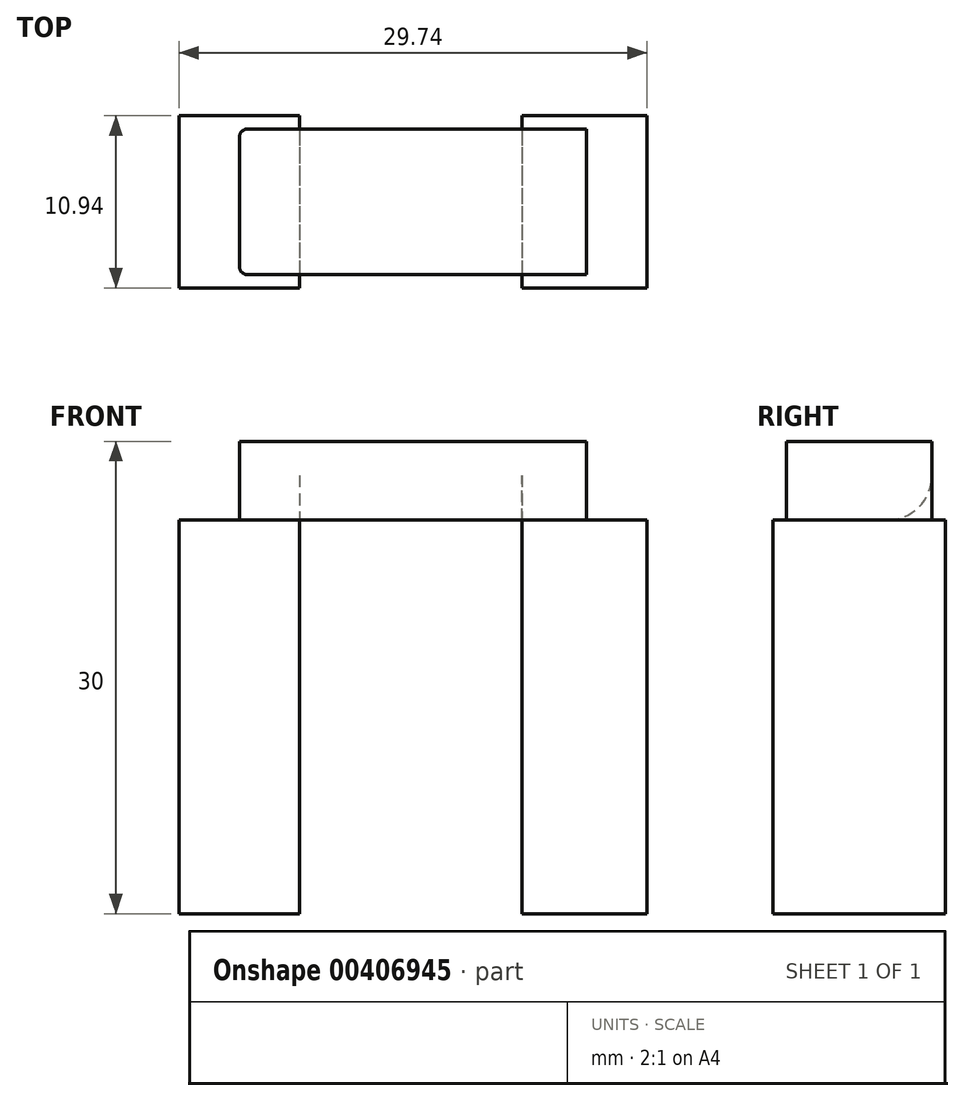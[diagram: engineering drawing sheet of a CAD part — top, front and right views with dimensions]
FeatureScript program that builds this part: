
annotation { "Feature Type Name" : "Feature", "Feature Type Description" : "" }
export const myFeature = defineFeature(function(context is Context, id is Id, definition is map)
    precondition{}
    {
        {
            var Q0;
            Q0=qCreatedBy(makeId("Top.planeOp"),FACE);
            var sketch = newSketch(context, id + "F0", { "sketchPlane" : qUnion([Q0])});
            skLineSegment(sketch, "E0.bottom", {"start": v(11.02, 4.62) * mm, "end": v(-11.02, 4.62) * mm});
            skLineSegment(sketch, "E0.top", {"start": v(11.02, -4.62) * mm, "end": v(-11.02, -4.62) * mm});
            skLineSegment(sketch, "E0.left", {"start": v(11.02, 4.62) * mm, "end": v(11.02, -4.62) * mm});
            skLineSegment(sketch, "E0.right", {"start": v(-11.02, 4.62) * mm, "end": v(-11.02, -4.62) * mm});
            skPoint(sketch, "E0.middle", {"position": v(0, 0) * mm});
            skLineSegment(sketch, "E1.bottom", {"start": v(14.87, 5.47) * mm, "end": v(-14.87, 5.47) * mm});
            skLineSegment(sketch, "E1.top", {"start": v(14.87, -5.47) * mm, "end": v(-14.87, -5.47) * mm});
            skLineSegment(sketch, "E1.left", {"start": v(14.87, 5.47) * mm, "end": v(14.87, -5.47) * mm});
            skLineSegment(sketch, "E1.right", {"start": v(-14.87, 5.47) * mm, "end": v(-14.87, -5.47) * mm});
            skLineSegment(sketch, "E2", {"start": v(-7.22, 5.47) * mm, "end": v(-7.22, -5.47) * mm});
            skLineSegment(sketch, "E3", {"start": v(6.91, 5.47) * mm, "end": v(6.91, -5.47) * mm});
            skSolve(sketch);
        }
        {
            var Q0;
            Q0=makeQuery(id+"F0.imprint","IMPRINT",FACE,{"disambiguationData":[TD([[makeQuery(id+"F0.imprint","IMPRINT",EDGE,{"derivedFrom":sQuery(id+"F0.wireOp",EDGE,"E0.bottom")}),1.0]])]});
            extrude(context, id + "F1", {"entities" : qUnion([Q0]), "depth" : 5 * mm});
        }
        {
            var Q0;
            {var subQ4=sQuery(id+"F0.wireOp",EDGE,"E0.right");Q0=makeQuery(id+"F0.imprint","IMPRINT",FACE,{"disambiguationData":[TD([[makeQuery(id+"F0.imprint","IMPRINT",EDGE,{"derivedFrom":subQ4}),-1.0]])]});}
            var Q1;
            {var subQ0=sQuery(id+"F0.wireOp",EDGE,"E0.left");Q1=makeQuery(id+"F0.imprint","IMPRINT",FACE,{"disambiguationData":[TD([[makeQuery(id+"F0.imprint","IMPRINT",EDGE,{"derivedFrom":subQ0}),1.0]])]});}
            var Q2;
            {var subQ0=sQuery(id+"F0.wireOp",EDGE,"E0.left");Q2=makeQuery(id+"F0.imprint","IMPRINT",FACE,{"disambiguationData":[TD([[makeQuery(id+"F0.imprint","IMPRINT",EDGE,{"derivedFrom":subQ0}),-1.0]])]});}
            var Q3;
            {var subQ0=sQuery(id+"F0.wireOp",EDGE,"E0.right");Q3=makeQuery(id+"F0.imprint","IMPRINT",FACE,{"disambiguationData":[TD([[makeQuery(id+"F0.imprint","IMPRINT",EDGE,{"derivedFrom":subQ0}),1.0]])]});}
            extrude(context, id + "F2", {"entities" : qUnion([Q0, Q1, Q2, Q3]), "operationType" : NewBodyOperationType.ADD, "oppositeDirection" : true, "depth" : 25 * mm});
        }
        {
            var Q0;
            Q0=makeQuery(id+"F1.opExtrude","SWEPT_EDGE",EDGE,{"disambiguationData":[OSD([sQuery(id+"F0.wireOp",EDGE,"E0.top"),sQuery(id+"F0.wireOp",EDGE,"E0.right")])]});
            var Q1;
            Q1=makeQuery(id+"F1.opExtrude","SWEPT_EDGE",EDGE,{"disambiguationData":[OSD([sQuery(id+"F0.wireOp",EDGE,"E0.bottom"),sQuery(id+"F0.wireOp",EDGE,"E0.right")])]});
            fillet(context, id + "F3", {"entities" : qUnion([Q0, Q1]), "radius" : 0.48 * mm, "tangentPropagation" : true, "allowEdgeOverflow" : false});
        }
        {
            var Q0;
            {var subQ0=sQuery(id+"F0.wireOp",EDGE,"E0.bottom");Q0=makeQuery(id+"F2.boolean.opBoolean","SPLIT",EDGE,{"disambiguationData":[topologyDisambiguationEdgeConnected([makeQuery(id+"F2.opExtrude","CAP_FACE",FACE,{"disambiguationData":[OSD([sQuery(id+"F0.wireOp",EDGE,"E1.bottom"),sQuery(id+"F0.wireOp",EDGE,"E1.top"),sQuery(id+"F0.wireOp",EDGE,"E1.right"),sQuery(id+"F0.wireOp",EDGE,"E2")])],"isStart":true})])],"derivedFrom":makeQuery(id+"F1.opExtrude","CAP_EDGE",EDGE,{"disambiguationData":[OSD([subQ0])],"isStart":true})});}
            fillet(context, id + "F4", {"entities" : qUnion([Q0]), "radius" : 2.85 * mm, "tangentPropagation" : true, "allowEdgeOverflow" : false});
        }
    });
